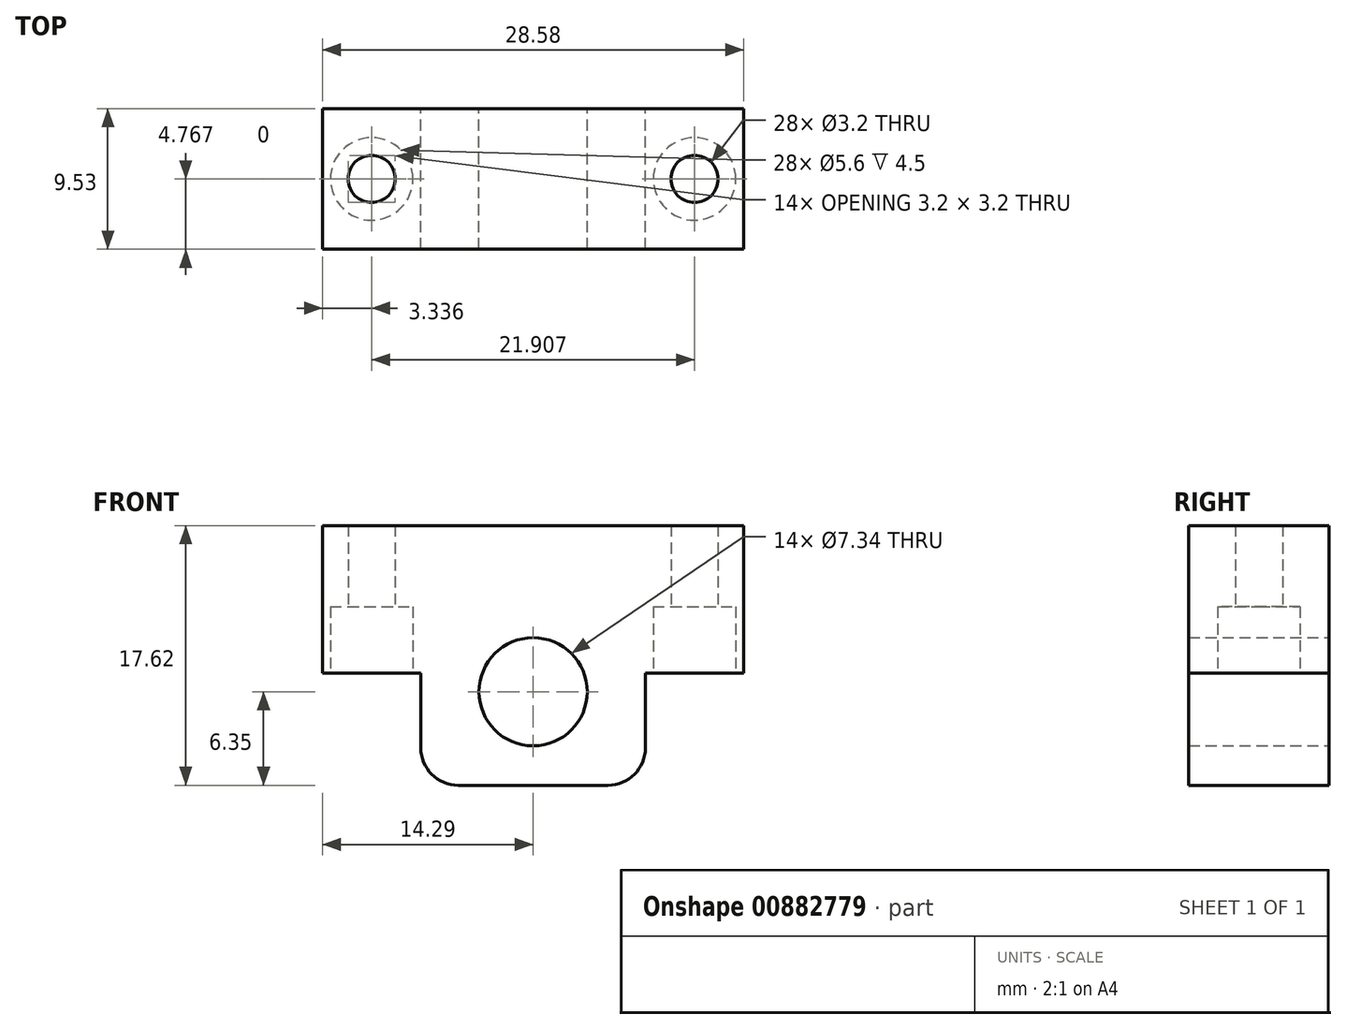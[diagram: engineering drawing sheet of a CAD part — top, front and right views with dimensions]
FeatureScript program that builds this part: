
annotation { "Feature Type Name" : "Feature", "Feature Type Description" : "" }
export const myFeature = defineFeature(function(context is Context, id is Id, definition is map)
    precondition{}
    {
        {
            var Q0;
            Q0=qCreatedBy(makeId("Front.planeOp"),FACE);
            var sketch = newSketch(context, id + "F0", { "sketchPlane" : qUnion([Q0])});
            skLineSegment(sketch, "E0.bottom", {"start": v(-14.29, 0) * mm, "end": v(-7.62, 0) * mm});
            skLineSegment(sketch, "E0.top", {"start": v(-14.29, 10) * mm, "end": v(14.29, 10) * mm});
            skLineSegment(sketch, "E0.left", {"start": v(-14.29, 0) * mm, "end": v(-14.29, 10) * mm});
            skLineSegment(sketch, "E0.right", {"start": v(14.29, 0) * mm, "end": v(14.29, 10) * mm});
            skLineSegment(sketch, "E1.top", {"start": v(-7.62, -7.62) * mm, "end": v(7.62, -7.62) * mm});
            skLineSegment(sketch, "E1.left", {"start": v(-7.62, 0) * mm, "end": v(-7.62, -7.62) * mm});
            skLineSegment(sketch, "E1.right", {"start": v(7.62, 0) * mm, "end": v(7.62, -7.62) * mm});
            skLineSegment(sketch, "E2.trimOffspring", {"start": v(7.62, 0) * mm, "end": v(14.29, 0) * mm});
            skLineSegment(sketch, "E3", {"start": v(0, 12.34) * mm, "end": v(0, -17.97) * mm});
            skCircle(sketch, "E4", {"center": v(0, -1.27) * mm, "radius": 3.67 * mm});
            skSolve(sketch);
        }
        {
            var Q0;
            Q0 = qSketchRegion(id + "F0", true);
            extrude(context, id + "F1", {"entities" : qUnion([Q0]), "depth" : 9.52 * mm, "offsetDistance" : 25.4 * mm});
        }
        {
            var Q0;
            Q0=makeQuery(id+"F1.opExtrude","SWEPT_FACE",FACE,{"disambiguationData":[OSD([sQuery(id+"F0.wireOp",EDGE,"E0.bottom")])]});
            var sketch = newSketch(context, id + "F2", { "sketchPlane" : qUnion([Q0])});
            skCircle(sketch, "E5", {"center": v(-10.95, 4.76) * mm, "radius": 1.6 * mm});
            skLineSegment(sketch, "E6", {"start": v(-10.95, 9.53) * mm, "end": v(-10.95, 0) * mm});
            skLineSegment(sketch, "E7", {"start": v(-14.29, 4.76) * mm, "end": v(-7.62, 4.76) * mm});
            skCircle(sketch, "E8.MirrorC", {"center": v(10.95, 4.76) * mm, "radius": 1.6 * mm});
            skSolve(sketch);
        }
        {
            var Q0;
            Q0 = qSketchRegion(id + "F2", true);
            extrude(context, id + "F3", {"entities" : qUnion([Q0]), "operationType" : NewBodyOperationType.REMOVE, "endBound" : BoundingType.UP_TO_NEXT, "oppositeDirection" : true, "depth" : 25.4 * mm, "offsetDistance" : 25.4 * mm});
        }
        {
            var Q0;
            Q0=makeQuery(id+"F1.opExtrude","SWEPT_EDGE",EDGE,{"disambiguationData":[OSD([sQuery(id+"F0.wireOp",EDGE,"E1.top"),sQuery(id+"F0.wireOp",EDGE,"E1.left")])]});
            var Q1;
            Q1=makeQuery(id+"F1.opExtrude","SWEPT_EDGE",EDGE,{"disambiguationData":[OSD([sQuery(id+"F0.wireOp",EDGE,"E1.top"),sQuery(id+"F0.wireOp",EDGE,"E1.right")])]});
            fillet(context, id + "F4", {"entities" : qUnion([Q0, Q1]), "radius" : 2.54 * mm, "tangentPropagation" : true, "allowEdgeOverflow" : false});
        }
        {
            var Q0;
            Q0=makeQuery(id+"F1.opExtrude","SWEPT_FACE",FACE,{"disambiguationData":[OSD([sQuery(id+"F0.wireOp",EDGE,"E0.bottom")])]});
            var sketch = newSketch(context, id + "F5", { "sketchPlane" : qUnion([Q0])});
            skCircle(sketch, "E9", {"center": v(-10.95, 4.76) * mm, "radius": 2.8 * mm});
            skCircle(sketch, "E10.MirrorC", {"center": v(10.95, 4.76) * mm, "radius": 2.8 * mm});
            skSolve(sketch);
        }
        {
            var Q0;
            Q0 = qSketchRegion(id + "F5", true);
            extrude(context, id + "F6", {"entities" : qUnion([Q0]), "operationType" : NewBodyOperationType.REMOVE, "oppositeDirection" : true, "depth" : 4.5 * mm, "offsetDistance" : 25.4 * mm});
        }
    });
